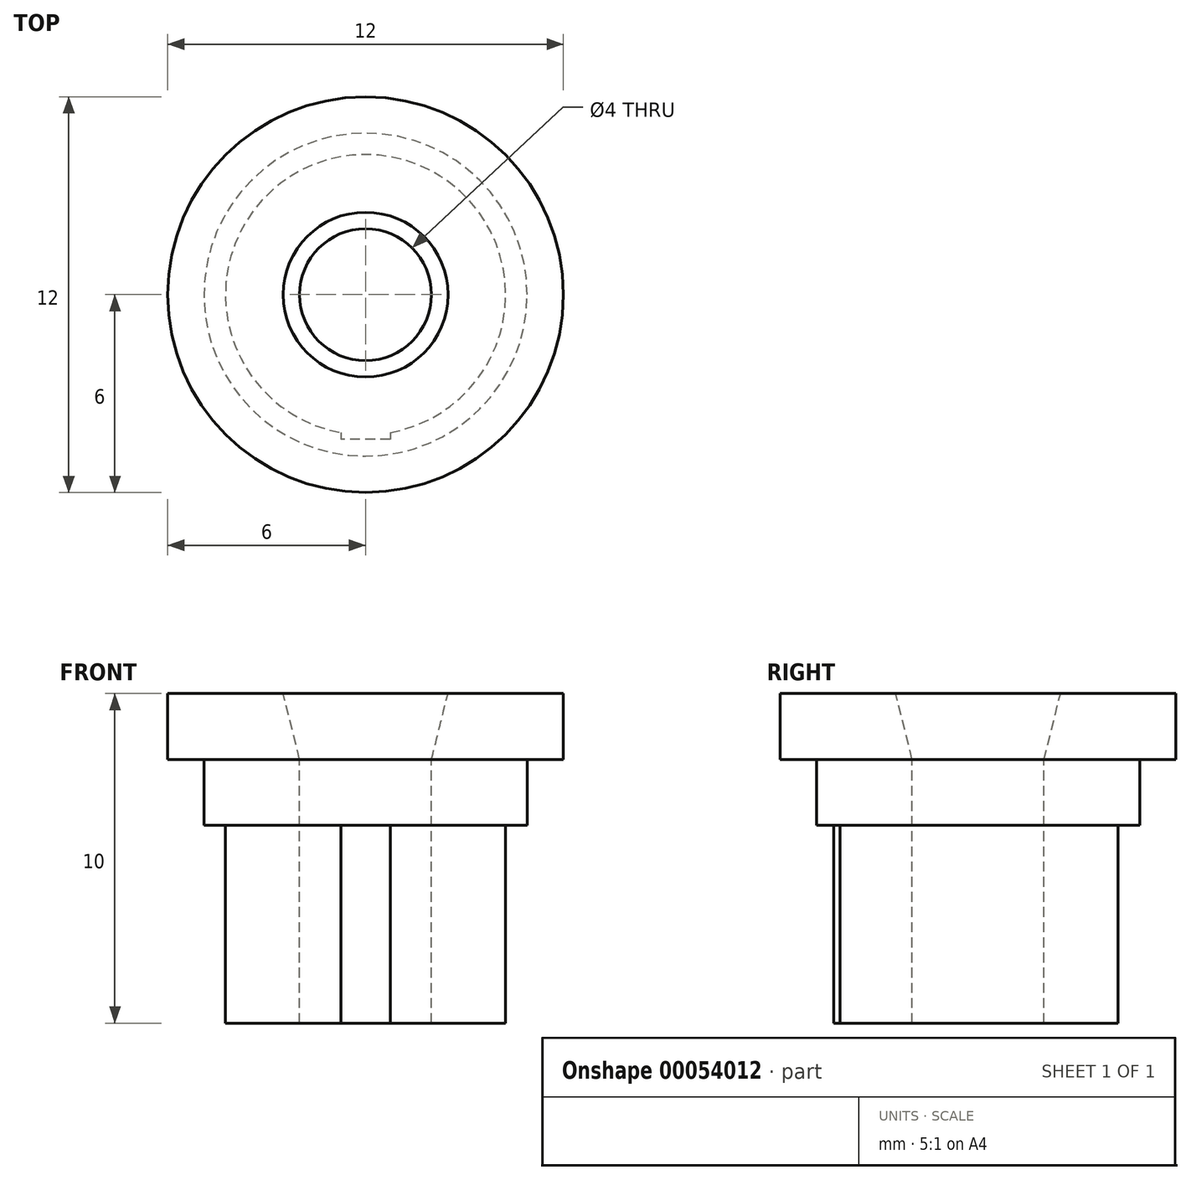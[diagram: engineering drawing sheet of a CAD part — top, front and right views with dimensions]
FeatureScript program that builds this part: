
annotation { "Feature Type Name" : "Feature", "Feature Type Description" : "" }
export const myFeature = defineFeature(function(context is Context, id is Id, definition is map)
    precondition{}
    {
        {
            var Q0;
            Q0=qCreatedBy(makeId("Front.planeOp"),FACE);
            var sketch = newSketch(context, id + "F0", { "sketchPlane" : qUnion([Q0])});
            skLineSegment(sketch, "E0", {"start": v(2.5, 0) * mm, "end": v(2, -2) * mm});
            skLineSegment(sketch, "E1", {"start": v(2, -2) * mm, "end": v(2, -10) * mm});
            skLineSegment(sketch, "E2", {"start": v(2, -10) * mm, "end": v(4.25, -10) * mm});
            skLineSegment(sketch, "E3", {"start": v(4.25, -10) * mm, "end": v(4.25, -4) * mm});
            skLineSegment(sketch, "E4", {"start": v(4.25, -4) * mm, "end": v(4.9, -4) * mm});
            skLineSegment(sketch, "E5", {"start": v(4.9, -4) * mm, "end": v(4.9, -2) * mm});
            skLineSegment(sketch, "E6", {"start": v(4.9, -2) * mm, "end": v(6, -2) * mm});
            skLineSegment(sketch, "E7", {"start": v(6, -2) * mm, "end": v(6, 0) * mm});
            skLineSegment(sketch, "E8", {"start": v(6, 0) * mm, "end": v(2.5, 0) * mm});
            skLineSegment(sketch, "E9", {"start": v(0, 0) * mm, "end": v(0, -24.4) * mm, "construction": true});
            skSolve(sketch);
        }
        {
            var Q0;
            Q0=makeQuery(id+"F0.imprint","IMPRINT",FACE,{"disambiguationData":[TD([[makeQuery(id+"F0.imprint","IMPRINT",EDGE,{"derivedFrom":sQuery(id+"F0.wireOp",EDGE,"E0")}),1.0]])]});
            var Q1;
            Q1=sQuery(id+"F0.wireOp",EDGE,"E9");
            revolve(context, id + "F1", {"entities" : qUnion([Q0]), "axis" : qUnion([Q1]), "revolveType" : RevolveType.FULL});
        }
        {
            var Q0;
            Q0=makeQuery(id+"F1.opRevolve","SWEPT_FACE",FACE,{"disambiguationData":[OSD([sQuery(id+"F0.wireOp",EDGE,"E2")])]});
            var sketch = newSketch(context, id + "F2", { "sketchPlane" : qUnion([Q0])});
            skLineSegment(sketch, "E10.bottom", {"start": v(0.75, 4.18) * mm, "end": v(-0.75, 4.18) * mm});
            skLineSegment(sketch, "E10.top", {"start": v(0.75, 4.38) * mm, "end": v(-0.75, 4.38) * mm});
            skLineSegment(sketch, "E10.left", {"start": v(0.75, 4.18) * mm, "end": v(0.75, 4.38) * mm});
            skLineSegment(sketch, "E10.right", {"start": v(-0.75, 4.18) * mm, "end": v(-0.75, 4.38) * mm});
            skPoint(sketch, "E10.middle", {"position": v(0, 4.28) * mm});
            skSolve(sketch);
        }
        {
            var Q0;
            Q0=makeQuery(id+"F2.imprint","IMPRINT",FACE,{"disambiguationData":[TD([[makeQuery(id+"F2.imprint","IMPRINT",EDGE,{"derivedFrom":sQuery(id+"F2.wireOp",EDGE,"E10.top")}),1.0]])]});
            extrude(context, id + "F3", {"entities" : qUnion([Q0]), "operationType" : NewBodyOperationType.ADD, "endBound" : BoundingType.UP_TO_NEXT, "oppositeDirection" : true, "depth" : 25 * mm});
        }
    });
